# Revit family: Railing_Ladder-Defender_BlueWater_Standard
name_source: partatom
category: Railings
units: mm (PartAtom-declared; Revit-internal decimal feet)

## family parameters
Always vertical = Yes
Cut with Voids When Loaded = No
Shared = No
Work Plane-Based = No

## types (3) — shared parameters
Building Codes = http://bluewater-mfg.com
Description = Hatch Guardrail
Gate Thickness = 0' - 1"
Green Building-LEED = https://www.arcat.com
Hardware Material = Steel - Galvanized - BlueWater
Height = 3' - 6"
Keynote = 05 52 00
Manufacturer = BlueWater
Manufacturer Website = http://bluewater-mfg.com
Revision = R1_2018-05
Sales Information = http://bluewater-mfg.com
URL = http://bluewater-mfg.com
Unit Width = 2' - 11 1/2"

## per-type parameters (varying)
| type | Model | Unit Depth |
| 5 - Standard | Ladder Defender 5 - Standard | 5' - 0" |
| 7-5 - Standard | Ladder Defender 7-5 - Standard | 7' - 6" |
| 10 - Standard | Ladder Defender 10 - Standard | 10' - 0" |

## geometry (parser evidence)
native form markers: Blend x36, Sweep x8
no freeform markers — native parametric forms only
